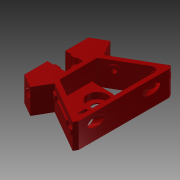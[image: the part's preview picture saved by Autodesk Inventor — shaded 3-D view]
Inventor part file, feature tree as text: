
AUTODESK INVENTOR PART (.ipt)
format: ipt  version: 2015 SP1 (Build 190203100, 203)  size: 575,488 bytes
history: native  units: mm
features: sketch x17, extrude x12, hole x5, reference x5, fillet x4, plane x4
ambient origin geometry x8: Origin, YZ Plane, XZ Plane, XY Plane, X Axis, Y Axis, Z Axis, Center Point
bodies: Solid2 (feature_tree)
feature tree (47):
  extrude  "Extrusion13"  Depth=55.0mm
  fillet  "Fillet5"  Radius=20.0mm
  extrude  "Extrusion2"  Depth=2.0mm
  extrude  "Extrusion7"  Depth=2.0mm
  plane  "Work Plane20"
  hole  "Hole2"  [1 undecoded]
  plane  "Work Plane21"
  hole  "Hole3"  [1 undecoded]
  plane  "Work Plane18"
  hole  "Hole7"  [1 undecoded]
  plane  "Work Plane19"
  hole  "Hole8"  [1 undecoded]
  fillet  "Fillet6"  Radius=20.0mm
  extrude  "Extrusion14"  Depth=3.0mm
  extrude  "Extrusion15"  Depth=3.0mm
  extrude  "Extrusion16"  TaperAngle=60.0deg  [1 undecoded]
  extrude  "Extrusion17"  TaperAngle=60.0deg  [1 undecoded]
  extrude  "Extrusion18"  Depth=1.5mm
  extrude  "Extrusion19"  Depth=20.0mm
  extrude  "Extrusion20"  Depth=8.0mm
  extrude  "Extrusion21"  Depth=10.0mm
  fillet  "Fillet7"  Radius=10.0mm
  extrude  "Extrusion22"  Depth=2.0mm
  fillet  "Fillet8"  Radius=10.0mm
  hole  "Hole9"  [1 undecoded]
  sketch  "Sketch1"  dims[d11=20.0mm d12=55.0mm d19=20.0mm]
  sketch  "Sketch2"  dims[d23=6.0mm d24=2.0mm]
  sketch  "Sketch8"  dims[d25=6.0mm d26=2.0mm]
  sketch  "Sketch9"  dims[d27=60.0mm d28=0.0mm d63=8.0mm d64=0.0mm]
  sketch  "Sketch10"  dims[d65=4.5mm d66=6.0mm d67=10.0mm d68=32.5mm d69=90.0deg d70=30.0mm d71=20.594885mm d73=35.0mm]
  sketch  "Sketch20"  dims[d74=35.0mm]
  sketch  "Sketch21"  dims[d78=4.5mm d79=6.0mm d80=10.0mm d81=32.5mm d82=90.0deg d83=8.0mm d84=20.594885mm d110=42.5mm]
  sketch  "Sketch22"  dims[d166=20.0mm d167=0.0mm d168=20.0mm d169=20.0mm]
  sketch  "Sketch23"  dims[d171=5.5mm d172=3.0mm]
  sketch  "Sketch24"  dims[d173=5.5mm d174=3.0mm]
  sketch  "Sketch25"  dims[d176=5.0mm d177=60.0deg]
  sketch  "Sketch26"  dims[d178=120.0deg d179=60.0deg]
  sketch  "Sketch27"  dims[d181=20.0mm d184=1.5mm]
  sketch  "Sketch28"  dims[d185=5.5mm d186=20.0mm]
  reference  "Reference2"
  reference  "Reference3"
  reference  "Reference4"
  reference  "Reference5"
  reference  "Reference6"
  sketch  "Sketch29"  dims[d188=4.5mm d189=6.0mm d190=8.0mm d191=16.35mm d192=90.0deg d193=8.0mm d194=20.594885mm d195=34.865485mm]
  sketch  "Sketch30"  dims[d197=4.5mm d198=6.0mm d199=8.0mm d200=16.35mm d201=90.0deg d202=8.0mm d203=20.594885mm d204=33.0mm d205=10.0mm]
  sketch  "Sketch31"  dims[d206=5.0mm d207=33.0mm d208=10.0mm d209=55.0mm d210=2.0mm d211=12.0mm d212=12.0mm d213=1.0mm d214=0.0mm d215=12.0mm d216=12.0mm d217=1.0mm d218=0.0mm d219=6.25mm d220=6.25mm d221=6.25mm d222=6.25mm d223=1.0mm d224=0.0mm d225=6.25mm d226=6.25mm d227=6.25mm d228=6.25mm d229=1.0mm d230=0.0mm d231=6.25mm d232=6.25mm d233=1.0mm d234=0.0mm d235=6.25mm d236=6.25mm d237=1.0mm d238=0.0mm d239=22.5mm d240=30.0mm d241=7.0mm d242=0.0mm d243=12.0mm d244=1.0mm d245=0.0mm d246=2.0mm d247=10.0mm d248=0.0mm d249=2.0mm d250=3.0mm d251=6.0mm d252=4.0mm d253=2.0mm d254=90.0deg d255=12.0mm d256=20.594885mm]
note: 7 required parameter values undecoded (feature->parameter linkage not recoverable at this tier; creation-order binding heuristic only, values carry confidence <= 0.55)
